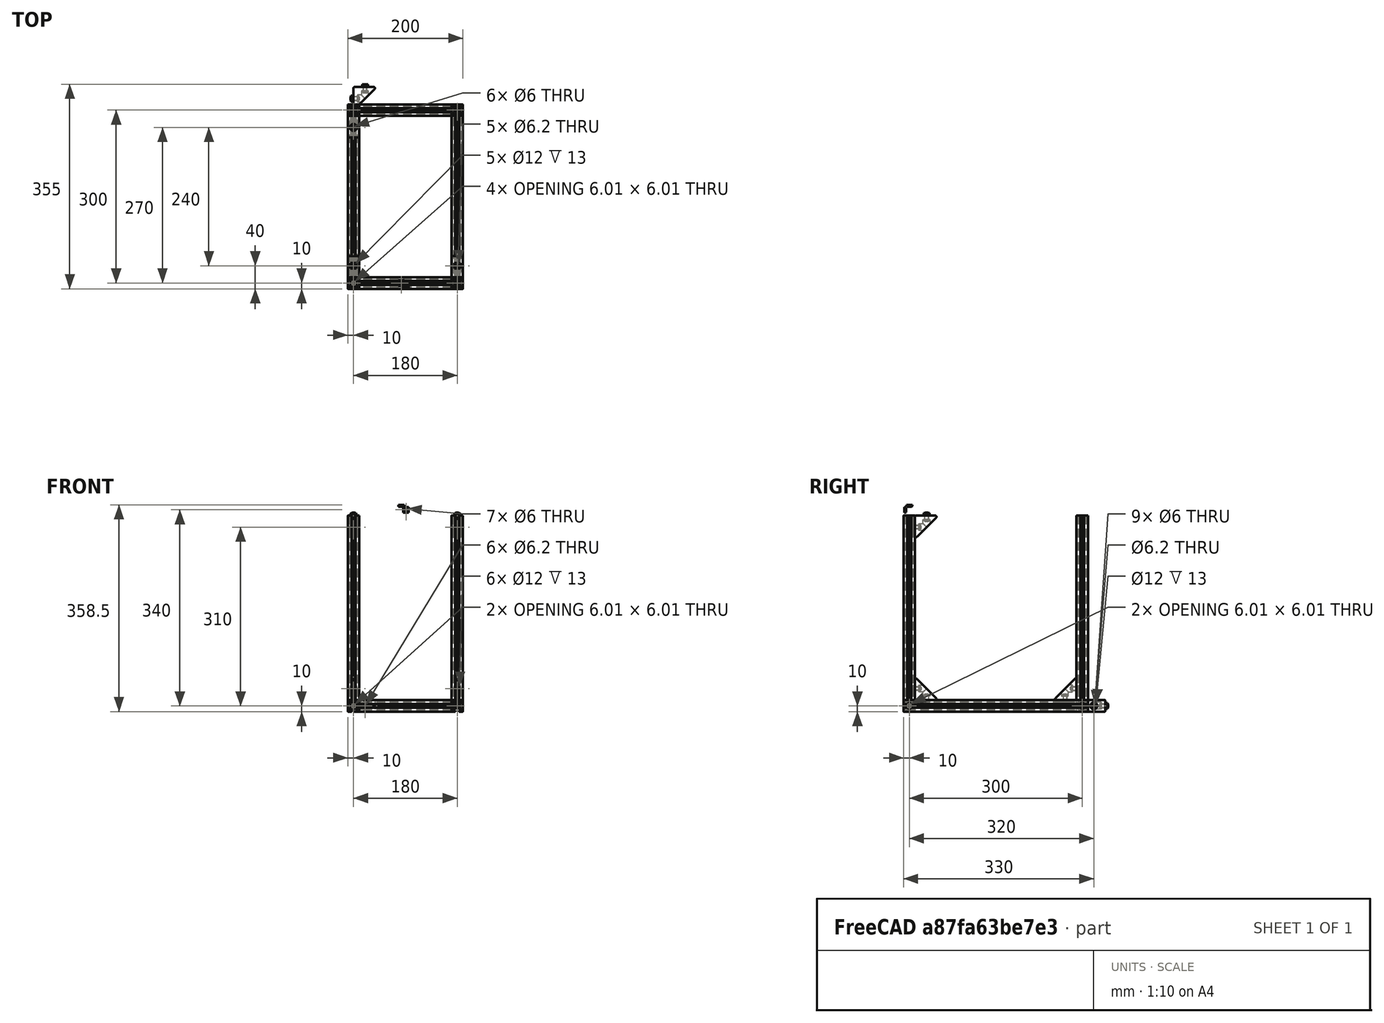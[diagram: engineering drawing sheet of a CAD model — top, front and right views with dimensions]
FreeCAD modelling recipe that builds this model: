
FCSTD DOCUMENT  (FreeCAD 0.17R9796 (Git))
Label: upperframe1
License: All rights reserved
LicenseURL: http://en.wikipedia.org/wiki/All_rights_reserved
objects: Part::Feature×51, Part::FeaturePython×16, App::Part×6, Part::Compound×5
note: 72 computed .brp shape members not serialized (recipe doc carries the construction recipe); baked Part::Feature solids carry a one-line shape summary decoded from their .brp

FEATURE [Part::Feature] Pocket003001  label="tslot32con"
  Placement = pos=(0,10,10) rot=(1,0,0;1.5708rad)
  shape: bbox 20 x 320 x 20 mm, 150 faces (baked)
FEATURE [Part::Feature] Pocket003002  label="tslot16"
  Placement = pos=(10,0,10) rot=(0,1,0;1.5708rad)
  shape: bbox 160 x 20 x 20 mm, 94 faces (baked)
FEATURE [Part::Feature] Pocket003006  label="tslot16_001"
  Placement = pos=(10,-300,10) rot=(0,1,0;1.5708rad)
  shape: bbox 160 x 20 x 20 mm, 94 faces (baked)
FEATURE [Part::Feature] Pocket003007  label="tslot32con_001"
  Placement = pos=(180,-310,10) rot=(0,0.707107,0.707107;3.14159rad)
  shape: bbox 20 x 320 x 20 mm, 150 faces (baked)
FEATURE [Part::FeaturePython] Screw  label="M6x25-Screw"  # Fasteners workbench fastener (typed FeaturePython)
  Placement = pos=(-4,0,10) rot=(0,-1,0;1.5708rad)
  diameter = 7
  invert = false
  length = 6
  matchOuter = false
  offset = 0
  thread = false
  type = 15
FEATURE [Part::FeaturePython] Screw001  label="M6x25-Screw004"  # Fasteners workbench fastener (typed FeaturePython)
  Placement = pos=(-4,-300,10) rot=(0,-1,0;1.5708rad)
  diameter = 7
  invert = false
  length = 6
  matchOuter = false
  offset = 0
  thread = false
  type = 15
FEATURE [Part::FeaturePython] Screw002  label="M6x25-Screw005"  # Fasteners workbench fastener (typed FeaturePython)
  Placement = pos=(184,0,10) rot=(0,1,0;1.5708rad)
  diameter = 7
  invert = false
  length = 6
  matchOuter = false
  offset = 0
  thread = false
  type = 15
FEATURE [Part::FeaturePython] Screw004  label="M6x25-Screw006"  # Fasteners workbench fastener (typed FeaturePython)
  Placement = pos=(184,-300,10) rot=(0,1,0;1.5708rad)
  diameter = 7
  invert = false
  length = 6
  matchOuter = false
  offset = 0
  thread = false
  type = 15
FEATURE [App::Part] Part  label="lower_frame"
  Group = -> [Pocket003001,Pocket003002,Pocket003006,Pocket003007,Screw,Screw001,Screw002,Screw004]
  License = CC BY 3.0
  LicenseURL = http://creativecommons.org/licenses/by/3.0/
  Origin = -> PartOrigin
FEATURE [Part::Feature] Pocket003008  label="tslot32con001"
  Placement = pos=(0,10,10) rot=(1,0,0;1.5708rad)
  shape: bbox 20 x 320 x 20 mm, 150 faces (baked)
FEATURE [Part::Feature] Pocket003009  label="tslot041"
  Placement = pos=(10,0,10) rot=(0,1,0;1.5708rad)
  shape: bbox 160 x 20 x 20 mm, 94 faces (baked)
FEATURE [Part::Feature] Pocket003010  label="tslot16_002"
  Placement = pos=(10,-300,10) rot=(0,1,0;1.5708rad)
  shape: bbox 160 x 20 x 20 mm, 94 faces (baked)
FEATURE [Part::Feature] Pocket003011  label="tslot32con_002"
  Placement = pos=(180,-310,10) rot=(0,0.707107,0.707107;3.14159rad)
  shape: bbox 20 x 320 x 20 mm, 150 faces (baked)
FEATURE [Part::FeaturePython] Screw005  label="M6x25-Screw007"  # Fasteners workbench fastener (typed FeaturePython)
  Placement = pos=(-4,0,10) rot=(0,-1,0;1.5708rad)
  diameter = 7
  invert = false
  length = 6
  matchOuter = false
  offset = 0
  thread = false
  type = 15
FEATURE [Part::FeaturePython] Screw006  label="M6x25-Screw008"  # Fasteners workbench fastener (typed FeaturePython)
  Placement = pos=(-4,-300,10) rot=(0,-1,0;1.5708rad)
  diameter = 7
  invert = false
  length = 6
  matchOuter = false
  offset = 0
  thread = false
  type = 15
FEATURE [Part::FeaturePython] Screw007  label="M6x25-Screw011"  # Fasteners workbench fastener (typed FeaturePython)
  Placement = pos=(184,0,10) rot=(0,1,0;1.5708rad)
  diameter = 7
  invert = false
  length = 6
  matchOuter = false
  offset = 0
  thread = false
  type = 15
FEATURE [Part::FeaturePython] Screw008  label="M6x25-Screw010"  # Fasteners workbench fastener (typed FeaturePython)
  Placement = pos=(184,-300,10) rot=(0,1,0;1.5708rad)
  diameter = 7
  invert = false
  length = 6
  matchOuter = false
  offset = 0
  thread = false
  type = 15
FEATURE [App::Part] Part001  label="upper_frame"
  Group = -> [Pocket003008,Pocket003009,Pocket003010,Pocket003011,Screw005,Screw006,Screw007,Screw008]
  License = CC BY 3.0
  LicenseURL = http://creativecommons.org/licenses/by/3.0/
  Origin = -> PartOrigin001
  Placement = pos=(0,0,340) rot=(0,0,1;0rad)
FEATURE [Part::Feature] Fillet004001  label="Fillet005"
  shape: bbox 37.5 x 37.5 x 20 mm, 26 faces (baked)
FEATURE [Part::FeaturePython] Screw009  label="M6x12-Screw"  # Fasteners workbench fastener (typed FeaturePython)
  Placement = pos=(7,20,10) rot=(0,1,0;1.5708rad)
  diameter = 4
  invert = false
  length = 1
  matchOuter = false
  offset = 0
  thread = false
  type = 20
FEATURE [Part::Feature] Body001  label="m6nutplate"
  Placement = pos=(-1.5,15,5) rot=(0,-1,0;1.5708rad)
  shape: bbox 3 x 10 x 10 mm, 9 faces (baked)
FEATURE [App::Part] Part002  label="cornerstonescrewnut"
  License = CC BY 3.0
  LicenseURL = http://creativecommons.org/licenses/by/3.0/
  Origin = -> PartOrigin002
  Placement = pos=(10,-50,20) rot=(0,-1,0;1.5708rad)
FEATURE [Part::FeaturePython] Screw010  label="M6x12-Screw001"  # Fasteners workbench fastener (typed FeaturePython)
  Placement = pos=(20,33,10) rot=(1,0,0;1.5708rad)
  diameter = 4
  invert = false
  length = 1
  matchOuter = false
  offset = 0
  thread = false
  type = 20
FEATURE [Part::Feature] Body002  label="m6nutplate001"
  Placement = pos=(15,41.5,5) rot=(0.57735,0.57735,0.57735;4.18879rad)
  shape: bbox 10 x 3 x 10 mm, 9 faces (baked)
FEATURE [Part::Feature] Fillet004002  label="Fillet006"
  shape: bbox 37.5 x 37.5 x 20 mm, 26 faces (baked)
FEATURE [Part::FeaturePython] Screw011  label="M6x12-Screw002"  # Fasteners workbench fastener (typed FeaturePython)
  Placement = pos=(7,20,10) rot=(0,1,0;1.5708rad)
  diameter = 4
  invert = false
  length = 1
  matchOuter = false
  offset = 0
  thread = false
  type = 20
FEATURE [Part::Feature] Body003  label="m6nutplate002"
  Placement = pos=(-1.5,15,5) rot=(0,-1,0;1.5708rad)
  shape: bbox 3 x 10 x 10 mm, 9 faces (baked)
FEATURE [Part::FeaturePython] Screw012  label="M6x12-Screw003"  # Fasteners workbench fastener (typed FeaturePython)
  Placement = pos=(20,33,10) rot=(1,0,0;1.5708rad)
  diameter = 4
  invert = false
  length = 1
  matchOuter = false
  offset = 0
  thread = false
  type = 20
FEATURE [Part::Feature] Body004  label="m6nutplate003"
  Placement = pos=(15,41.5,5) rot=(0.57735,0.57735,0.57735;4.18879rad)
  shape: bbox 10 x 3 x 10 mm, 9 faces (baked)
FEATURE [App::Part] Part003  label="cornerstonescrewnut001"
  Group = -> [Body003,Screw011,Fillet004002,Screw012,Body004,PartOrigin002,Body001,Screw009,Fillet004001,Screw010,Body002,Part002]
  License = CC BY 3.0
  LicenseURL = http://creativecommons.org/licenses/by/3.0/
  Origin = -> PartOrigin003
  Placement = pos=(190,-50,20) rot=(0,-1,0;1.5708rad)
FEATURE [Part::Feature] Fillet004003  label="Fillet007"
  shape: bbox 37.5 x 37.5 x 20 mm, 26 faces (baked)
FEATURE [Part::FeaturePython] Screw013  label="M6x12-Screw004"  # Fasteners workbench fastener (typed FeaturePython)
  Placement = pos=(7,20,10) rot=(0,1,0;1.5708rad)
  diameter = 4
  invert = false
  length = 1
  matchOuter = false
  offset = 0
  thread = false
  type = 20
FEATURE [Part::Feature] Body005  label="m6nutplate004"
  Placement = pos=(-1.5,15,5) rot=(0,-1,0;1.5708rad)
  shape: bbox 3 x 10 x 10 mm, 9 faces (baked)
FEATURE [Part::FeaturePython] Screw014  label="M6x12-Screw005"  # Fasteners workbench fastener (typed FeaturePython)
  Placement = pos=(20,33,10) rot=(1,0,0;1.5708rad)
  diameter = 4
  invert = false
  length = 1
  matchOuter = false
  offset = 0
  thread = false
  type = 20
FEATURE [Part::Feature] Body006  label="m6nutplate005"
  Placement = pos=(15,41.5,5) rot=(0.57735,0.57735,0.57735;4.18879rad)
  shape: bbox 10 x 3 x 10 mm, 9 faces (baked)
FEATURE [App::Part] Part004  label="cornerstonescrewnut002"
  Group = -> [Body005,Screw013,Fillet004003,Screw014,Body006]
  License = CC BY 3.0
  LicenseURL = http://creativecommons.org/licenses/by/3.0/
  Origin = -> PartOrigin004
  Placement = pos=(-10,-50,340) rot=(0,1,0;1.5708rad)
FEATURE [Part::Feature] Fillet004004  label="Fillet008"
  shape: bbox 37.5 x 37.5 x 20 mm, 26 faces (baked)
FEATURE [Part::FeaturePython] Screw015  label="M6x12-Screw006"  # Fasteners workbench fastener (typed FeaturePython)
  Placement = pos=(7,20,10) rot=(0,1,0;1.5708rad)
  diameter = 4
  invert = false
  length = 1
  matchOuter = false
  offset = 0
  thread = false
  type = 20
FEATURE [Part::Feature] Body007  label="m6nutplate006"
  Placement = pos=(-1.5,15,5) rot=(0,-1,0;1.5708rad)
  shape: bbox 3 x 10 x 10 mm, 9 faces (baked)
FEATURE [Part::FeaturePython] Screw016  label="M6x12-Screw007"  # Fasteners workbench fastener (typed FeaturePython)
  Placement = pos=(20,33,10) rot=(1,0,0;1.5708rad)
  diameter = 4
  invert = false
  length = 1
  matchOuter = false
  offset = 0
  thread = false
  type = 20
FEATURE [Part::Feature] Body008  label="m6nutplate007"
  Placement = pos=(15,41.5,5) rot=(0.57735,0.57735,0.57735;4.18879rad)
  shape: bbox 10 x 3 x 10 mm, 9 faces (baked)
FEATURE [App::Part] Part005  label="cornerstonescrewnut003"
  Group = -> [Body007,Screw015,Fillet004004,Screw016,Body008]
  License = CC BY 3.0
  LicenseURL = http://creativecommons.org/licenses/by/3.0/
  Origin = -> PartOrigin005
  Placement = pos=(170,-50,340) rot=(0,1,0;1.5708rad)
FEATURE [Part::Feature] Body009001  label="m6nutplate010"
  Placement = pos=(-1.5,15,5) rot=(0,-1,0;1.5708rad)
  shape: bbox 3 x 10 x 10 mm, 9 faces (baked)
FEATURE [Part::Feature] Body010001  label="m6nutplate011"
  Placement = pos=(15,41.5,5) rot=(0.57735,0.57735,0.57735;4.18879rad)
  shape: bbox 10 x 3 x 10 mm, 9 faces (baked)
FEATURE [Part::Feature] Screw018001  label="M6x12-Screw010"
  Placement = pos=(20,33,10) rot=(1,0,0;1.5708rad)
  shape: bbox 10.5 x 15.3 x 10.5 mm, 15 faces (baked)
FEATURE [Part::Feature] Screw017001  label="M6x12-Screw011"
  Placement = pos=(7,20,10) rot=(0,1,0;1.5708rad)
  shape: bbox 15.3 x 10.5 x 10.5 mm, 15 faces (baked)
FEATURE [Part::Feature] Fillet004005001  label="Fillet010"
  shape: bbox 37.5 x 37.5 x 20 mm, 26 faces (baked)
FEATURE [Part::Compound] Compound
  Links = -> [Body009001,Fillet004005001,Screw017001,Body010001,Screw018001]
  Placement = pos=(10,-250,340) rot=(0.707107,0,-0.707107;3.14159rad)
FEATURE [Part::Feature] Body010002  label="m6nutplate012"
  Placement = pos=(-1.5,15,5) rot=(0,-1,0;1.5708rad)
  shape: bbox 3 x 10 x 10 mm, 9 faces (baked)
FEATURE [Part::Feature] Body010003  label="m6nutplate013"
  Placement = pos=(15,41.5,5) rot=(0.57735,0.57735,0.57735;4.18879rad)
  shape: bbox 10 x 3 x 10 mm, 9 faces (baked)
FEATURE [Part::Feature] Screw018002  label="M6x12-Screw012"
  Placement = pos=(20,33,10) rot=(1,0,0;1.5708rad)
  shape: bbox 10.5 x 15.3 x 10.5 mm, 15 faces (baked)
FEATURE [Part::Feature] Screw018003  label="M6x12-Screw013"
  Placement = pos=(7,20,10) rot=(0,1,0;1.5708rad)
  shape: bbox 15.3 x 10.5 x 10.5 mm, 15 faces (baked)
FEATURE [Part::Feature] Fillet004005002  label="Fillet011"
  shape: bbox 37.5 x 37.5 x 20 mm, 26 faces (baked)
FEATURE [Part::Compound] Compound001
  Links = -> [Body010002,Fillet004005002,Screw018003,Body010003,Screw018002]
  Placement = pos=(190,-250,340) rot=(0.707107,0,-0.707107;3.14159rad)
FEATURE [Part::Feature] Body010004  label="m6nutplate014"
  Placement = pos=(-1.5,15,5) rot=(0,-1,0;1.5708rad)
  shape: bbox 3 x 10 x 10 mm, 9 faces (baked)
FEATURE [Part::Feature] Body010005  label="m6nutplate015"
  Placement = pos=(15,41.5,5) rot=(0.57735,0.57735,0.57735;4.18879rad)
  shape: bbox 10 x 3 x 10 mm, 9 faces (baked)
FEATURE [Part::Feature] Screw018004  label="M6x12-Screw014"
  Placement = pos=(20,33,10) rot=(1,0,0;1.5708rad)
  shape: bbox 10.5 x 15.3 x 10.5 mm, 15 faces (baked)
FEATURE [Part::Feature] Screw018005  label="M6x12-Screw015"
  Placement = pos=(7,20,10) rot=(0,1,0;1.5708rad)
  shape: bbox 15.3 x 10.5 x 10.5 mm, 15 faces (baked)
FEATURE [Part::Feature] Fillet004005003  label="Fillet012"
  shape: bbox 37.5 x 37.5 x 20 mm, 26 faces (baked)
FEATURE [Part::Compound] Compound002
  Links = -> [Body010004,Fillet004005003,Screw018005,Body010005,Screw018004]
  Placement = pos=(10,-290,60) rot=(0.57735,0.57735,-0.57735;4.18879rad)
FEATURE [Part::Feature] Body010006  label="m6nutplate016"
  Placement = pos=(-1.5,15,5) rot=(0,-1,0;1.5708rad)
  shape: bbox 3 x 10 x 10 mm, 9 faces (baked)
FEATURE [Part::Feature] Body010007  label="m6nutplate017"
  Placement = pos=(15,41.5,5) rot=(0.57735,0.57735,0.57735;4.18879rad)
  shape: bbox 10 x 3 x 10 mm, 9 faces (baked)
FEATURE [Part::Feature] Screw018006  label="M6x12-Screw016"
  Placement = pos=(20,33,10) rot=(1,0,0;1.5708rad)
  shape: bbox 10.5 x 15.3 x 10.5 mm, 15 faces (baked)
FEATURE [Part::Feature] Screw018007  label="M6x12-Screw017"
  Placement = pos=(7,20,10) rot=(0,1,0;1.5708rad)
  shape: bbox 15.3 x 10.5 x 10.5 mm, 15 faces (baked)
FEATURE [Part::Feature] Fillet004005004  label="Fillet013"
  shape: bbox 37.5 x 37.5 x 20 mm, 26 faces (baked)
FEATURE [Part::Compound] Compound003
  Links = -> [Body010006,Fillet004005004,Screw018007,Body010007,Screw018006]
  Placement = pos=(190,-290,60) rot=(0.57735,0.57735,-0.57735;4.18879rad)
FEATURE [Part::Feature] Pocket001001  label="tslot32"
  Placement = pos=(0,0,20) rot=(0,0,1;0rad)
  shape: bbox 20 x 20 x 320 mm, 94 faces (baked)
FEATURE [Part::Feature] Body010008  label="m6nutplate018"
  Placement = pos=(-1.5,15,5) rot=(0,-1,0;1.5708rad)
  shape: bbox 3 x 10 x 10 mm, 9 faces (baked)
FEATURE [Part::Feature] Body010009  label="m6nutplate019"
  Placement = pos=(15,41.5,5) rot=(0.57735,0.57735,0.57735;4.18879rad)
  shape: bbox 10 x 3 x 10 mm, 9 faces (baked)
FEATURE [Part::Feature] Screw018008  label="M6x12-Screw018"
  Placement = pos=(20,33,10) rot=(1,0,0;1.5708rad)
  shape: bbox 10.5 x 15.3 x 10.5 mm, 15 faces (baked)
FEATURE [Part::Feature] Screw018009  label="M6x12-Screw019"
  Placement = pos=(7,20,10) rot=(0,1,0;1.5708rad)
  shape: bbox 15.3 x 10.5 x 10.5 mm, 15 faces (baked)
FEATURE [Part::Feature] Fillet004005005  label="Fillet014"
  shape: bbox 37.5 x 37.5 x 20 mm, 26 faces (baked)
FEATURE [Part::Compound] Compound004
  Links = -> [Body010008,Fillet004005005,Screw018009,Body010009,Screw018008]
  Placement = pos=(-10,-10,60) rot=(0.57735,-0.57735,0.57735;4.18879rad)
FEATURE [Part::Feature] Pocket003012  label="tslot32_001"
  Placement = pos=(0,-300,20) rot=(0,0,1;0rad)
  shape: bbox 20 x 20 x 320 mm, 94 faces (baked)
FEATURE [Part::Feature] Pocket003013  label="tslot32_002"
  Placement = pos=(180,0,20) rot=(0,0,1;0rad)
  shape: bbox 20 x 20 x 320 mm, 94 faces (baked)
FEATURE [Part::Feature] Pocket003014  label="tslot32_003"
  Placement = pos=(180,-300,20) rot=(0,0,1;0rad)
  shape: bbox 20 x 20 x 320 mm, 94 faces (baked)
FEATURE [Part::Feature] Chamfer001001  label="m6nutplate020"
  Placement = pos=(88,-295,358.5) rot=(-0.707107,0.707107,0;3.14159rad)
  shape: bbox 10 x 10 x 3 mm, 9 faces (baked)
FEATURE [Part::Feature] Chamfer001002  label="m6nutplate021"
  Placement = pos=(96,-308.5,355) rot=(0.57735,-0.57735,-0.57735;4.18879rad)
  shape: bbox 10 x 3 x 10 mm, 9 faces (baked)
